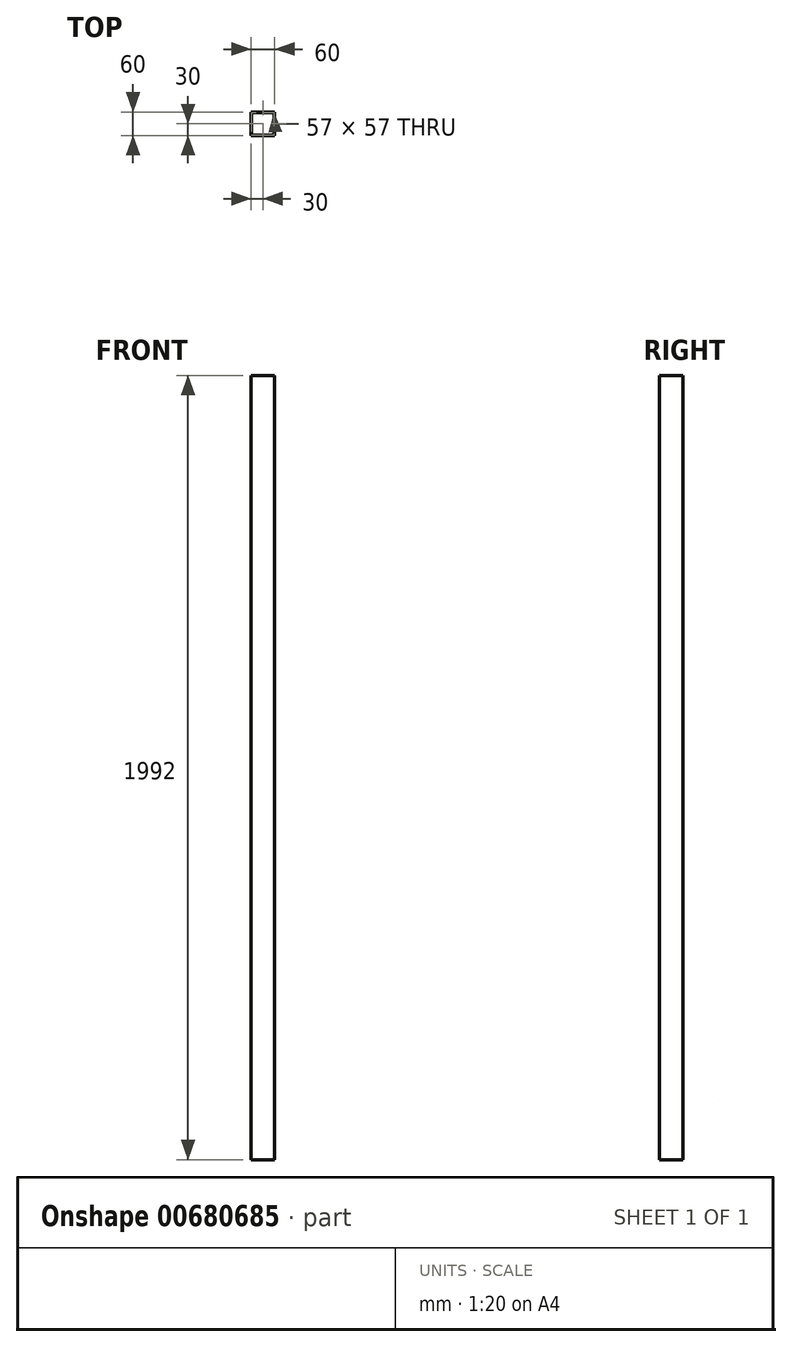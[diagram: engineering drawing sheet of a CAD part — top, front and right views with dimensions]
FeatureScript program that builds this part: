
annotation { "Feature Type Name" : "Feature", "Feature Type Description" : "" }
export const myFeature = defineFeature(function(context is Context, id is Id, definition is map)
    precondition{}
    {
        {
            var Q0;
            Q0=qCreatedBy(makeId("Top.planeOp"),FACE);
            var sketch = newSketch(context, id + "F0", { "sketchPlane" : qUnion([Q0])});
            skLineSegment(sketch, "E0.bottom", {"start": v(28.5, 28.5) * mm, "end": v(-28.5, 28.5) * mm});
            skLineSegment(sketch, "E0.top", {"start": v(28.5, -28.5) * mm, "end": v(-28.5, -28.5) * mm});
            skLineSegment(sketch, "E0.left", {"start": v(28.5, 28.5) * mm, "end": v(28.5, -28.5) * mm});
            skLineSegment(sketch, "E0.right", {"start": v(-28.5, 28.5) * mm, "end": v(-28.5, -28.5) * mm});
            skPoint(sketch, "E0.middle", {"position": v(0, 0) * mm});
            skLineSegment(sketch, "E1.bottom", {"start": v(30, 30) * mm, "end": v(-30, 30) * mm});
            skLineSegment(sketch, "E1.top", {"start": v(30, -30) * mm, "end": v(-30, -30) * mm});
            skLineSegment(sketch, "E1.left", {"start": v(30, 30) * mm, "end": v(30, -30) * mm});
            skLineSegment(sketch, "E1.right", {"start": v(-30, 30) * mm, "end": v(-30, -30) * mm});
            skSolve(sketch);
        }
        {
            var Q0;
            Q0=makeQuery(id+"F0.imprint","IMPRINT",FACE,{"disambiguationData":[TD([[makeQuery(id+"F0.imprint","IMPRINT",EDGE,{"derivedFrom":sQuery(id+"F0.wireOp",EDGE,"E0.bottom")}),-1.0]])]});
            extrude(context, id + "F1", {"entities" : qUnion([Q0]), "endBound" : BoundingType.SYMMETRIC, "depth" : (1998 - 6) * mm, "offsetDistance" : 25 * mm});
        }
    });
